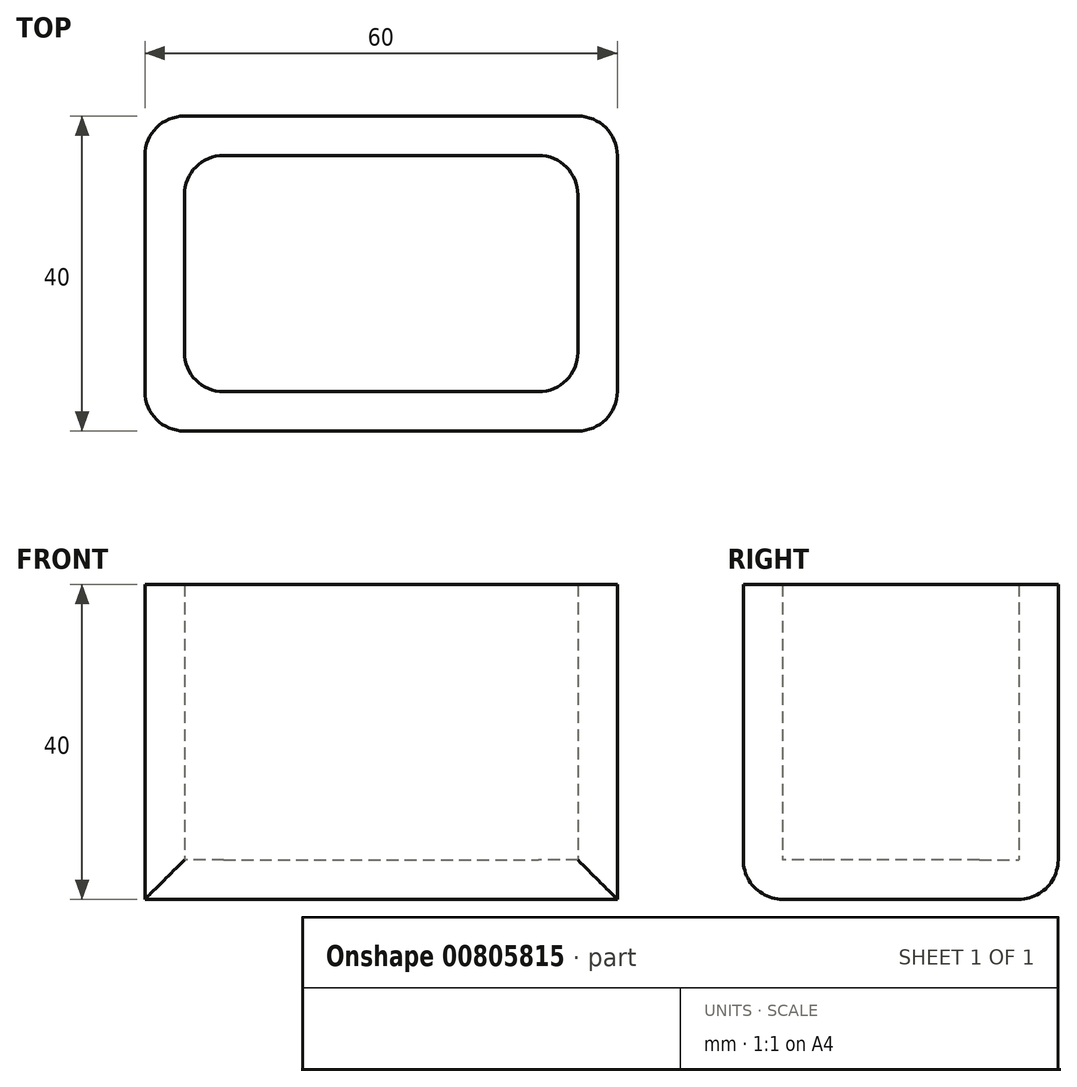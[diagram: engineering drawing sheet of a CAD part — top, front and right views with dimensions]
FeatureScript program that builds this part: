
annotation { "Feature Type Name" : "Feature", "Feature Type Description" : "" }
export const myFeature = defineFeature(function(context is Context, id is Id, definition is map)
    precondition{}
    {
        {
            var Q0;
            Q0=qCreatedBy(makeId("Top.planeOp"),FACE);
            var sketch = newSketch(context, id + "F0", { "sketchPlane" : qUnion([Q0])});
            skLineSegment(sketch, "E0.bottom", {"start": v(-30, 20) * mm, "end": v(30, 20) * mm});
            skLineSegment(sketch, "E0.top", {"start": v(-30, -20) * mm, "end": v(30, -20) * mm});
            skLineSegment(sketch, "E0.left", {"start": v(-30, 20) * mm, "end": v(-30, -20) * mm});
            skLineSegment(sketch, "E0.right", {"start": v(30, 20) * mm, "end": v(30, -20) * mm});
            skPoint(sketch, "E0.middle", {"position": v(0, 0) * mm});
            skSolve(sketch);
        }
        {
            var Q0;
            Q0 = qSketchRegion(id + "F0", true);
            extrude(context, id + "F1", {"entities" : qUnion([Q0]), "depth" : 40 * mm, "offsetDistance" : 25 * mm});
        }
        {
            var Q0;
            Q0=makeQuery(id+"F1.opExtrude","CAP_FACE",FACE,{"disambiguationData":[OSD([sQuery(id+"F0.wireOp",EDGE,"E0.bottom"),sQuery(id+"F0.wireOp",EDGE,"E0.top"),sQuery(id+"F0.wireOp",EDGE,"E0.left"),sQuery(id+"F0.wireOp",EDGE,"E0.right")])],"isStart":false});
            shell(context, id + "F2", {"entities" : qUnion([Q0]), "thickness" : 5 * mm});
        }
        {
            var Q0;
            Q0=makeQuery(id+"F1.opExtrude","SWEPT_EDGE",EDGE,{"disambiguationData":[OSD([sQuery(id+"F0.wireOp",EDGE,"E0.bottom"),sQuery(id+"F0.wireOp",EDGE,"E0.left")])]});
            var Q1;
            Q1=makeQuery(id+"F1.opExtrude","SWEPT_EDGE",EDGE,{"disambiguationData":[OSD([sQuery(id+"F0.wireOp",EDGE,"E0.bottom"),sQuery(id+"F0.wireOp",EDGE,"E0.right")])]});
            var Q2;
            Q2=makeQuery(id+"F1.opExtrude","SWEPT_EDGE",EDGE,{"disambiguationData":[OSD([sQuery(id+"F0.wireOp",EDGE,"E0.top"),sQuery(id+"F0.wireOp",EDGE,"E0.left")])]});
            var Q3;
            Q3=makeQuery(id+"F1.opExtrude","SWEPT_EDGE",EDGE,{"disambiguationData":[OSD([sQuery(id+"F0.wireOp",EDGE,"E0.top"),sQuery(id+"F0.wireOp",EDGE,"E0.right")])]});
            var Q4;
            Q4=makeQuery(id+"F2.opShell","OFFSET_EDGE",EDGE,{"disambiguationData":[OSD([sQuery(id+"F0.wireOp",EDGE,"E0.top"),sQuery(id+"F0.wireOp",EDGE,"E0.left")])]});
            var Q5;
            Q5=makeQuery(id+"F2.opShell","OFFSET_EDGE",EDGE,{"disambiguationData":[OSD([sQuery(id+"F0.wireOp",EDGE,"E0.bottom"),sQuery(id+"F0.wireOp",EDGE,"E0.left")])]});
            var Q6;
            Q6=makeQuery(id+"F2.opShell","OFFSET_EDGE",EDGE,{"disambiguationData":[OSD([sQuery(id+"F0.wireOp",EDGE,"E0.top"),sQuery(id+"F0.wireOp",EDGE,"E0.right")])]});
            var Q7;
            Q7=makeQuery(id+"F2.opShell","OFFSET_EDGE",EDGE,{"disambiguationData":[OSD([sQuery(id+"F0.wireOp",EDGE,"E0.bottom"),sQuery(id+"F0.wireOp",EDGE,"E0.right")])]});
            var Q8;
            Q8=makeQuery(id+"F1.opExtrude","CAP_EDGE",EDGE,{"disambiguationData":[OSD([sQuery(id+"F0.wireOp",EDGE,"E0.bottom")])],"isStart":true});
            var Q9;
            Q9=makeQuery(id+"F1.opExtrude","CAP_EDGE",EDGE,{"disambiguationData":[OSD([sQuery(id+"F0.wireOp",EDGE,"E0.top")])],"isStart":true});
            fillet(context, id + "F3", {"entities" : qUnion([Q0, Q1, Q2, Q3, Q4, Q5, Q6, Q7, Q8, Q9]), "radius" : 5 * mm, "tangentPropagation" : true, "allowEdgeOverflow" : false});
        }
    });
